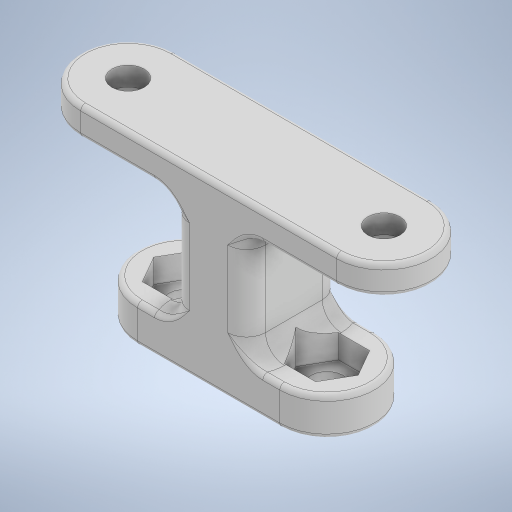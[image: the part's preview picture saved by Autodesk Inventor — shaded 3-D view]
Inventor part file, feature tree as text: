
AUTODESK INVENTOR PART (.ipt)
format: ipt  version: 2024.2 (Build 282272000, 272)  size: 421,376 bytes
history: native  units: mm
features: extrude x6, sketch x6, fillet x2
ambient origin geometry x8: Origin, YZ Plane, XZ Plane, XY Plane, X Axis, Y Axis, Z Axis, Center Point
bodies: Solid1 (feature_tree)
feature tree (14):
  extrude  "Extrusion1"  Depth=27.0mm
  extrude  "Extrusion2"  Depth=10.0mm TaperAngle=0.0deg
  extrude  "Extrusion3"  Depth=15.0mm
  extrude  "Extrusion4"  Depth=5.7mm
  extrude  "Extrusion5"  Depth=3.4mm
  extrude  "Extrusion6"  Depth=0.5mm
  fillet  "Fillet3"  Radius=1.0mm
  fillet  "Fillet2"  Radius=0.5mm
  sketch  "Sketch1"  dims[d0=3.4mm d1=27.0mm]
  sketch  "Sketch2"  dims[d2=10.0mm d3=3.0mm d4=0.0mm]
  sketch  "Sketch3"  dims[d5=12.0mm d6=0.0mm d7=15.0mm]
  sketch  "Sketch4"  dims[d8=4.0mm d9=0.0mm d10=5.7mm]
  sketch  "Sketch5"  dims[d11=2.5mm d12=0.0mm d13=3.4mm]
  sketch  "Sketch6"  dims[d14=2.0mm d15=0.0mm d16=5.1mm d17=1.0mm d18=0.0mm d20=0.5mm d22=8.0mm d23=2.0mm]
